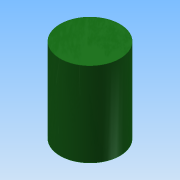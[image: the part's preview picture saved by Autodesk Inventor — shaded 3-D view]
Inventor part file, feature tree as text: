
AUTODESK INVENTOR PART (.ipt)
format: ipt  version: 2015 (Build 190159000, 159)  size: 80,384 bytes
history: native  units: mm
features: extrude x1, sketch x1
ambient origin geometry x8: Origin, YZ Plane, XZ Plane, XY Plane, X Axis, Y Axis, Z Axis, Center Point
bodies: Volumenkörper1 (feature_tree)
feature tree (2):
  extrude  "Extrusion1"  Depth=14.8mm TaperAngle=0.0deg
  sketch  "Skizze1"  dims[d0=10.5mm d1=14.8mm d2=0.0mm]
